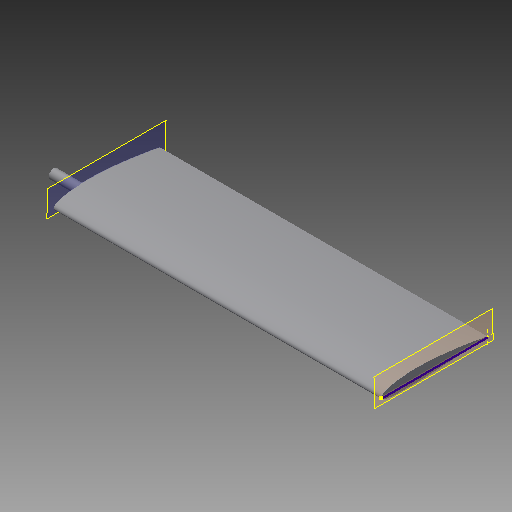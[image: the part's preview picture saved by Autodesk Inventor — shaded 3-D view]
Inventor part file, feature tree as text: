
AUTODESK INVENTOR PART (.ipt)
format: ipt  version: 2018 (Build 220112000, 112)  size: 116,736 bytes
history: native  units: in
note: dims shown in document units (in); Inventor stores cm internally (conversion verified against a paired STEP export)
features: sketch x3, plane x3, extrude x2, mirror x1
ambient origin geometry x8: Origin, YZ Plane, XZ Plane, XY Plane, X Axis, Y Axis, Z Axis, Center Point
bodies: Solid1 (feature_tree)
feature tree (9):
  extrude  "Extrusion1"  [1 undecoded]
  sketch  "Sketch2"  dims[d3=1.0in d4=2.9134in d5=0.0in]
  plane  "Work Plane1"
  plane  "Work Plane2"
  mirror  "Mirror1"
  extrude  "Extrusion2"  Depth=2.9134in TaperAngle=0.0deg
  sketch  "Sketch1"  dims[d0=33.8583in d1=0.0in d2=-0.0137in]
  plane  "Work Plane3"
  sketch  "Sketch3"
note: 1 required parameter value undecoded (feature->parameter linkage not recoverable at this tier; creation-order binding heuristic only, values carry confidence <= 0.55)
